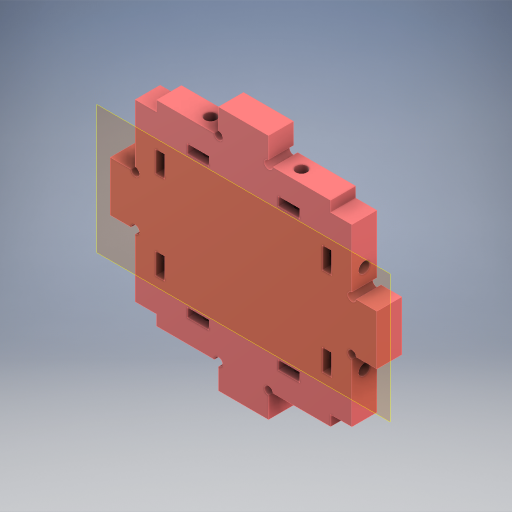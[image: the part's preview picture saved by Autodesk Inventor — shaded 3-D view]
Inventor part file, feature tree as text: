
AUTODESK INVENTOR PART (.ipt)
format: ipt  version: 2024 (Build 280153000, 153)  size: 487,936 bytes
history: native  units: in
note: dims shown in document units (in); Inventor stores cm internally (conversion verified against a paired STEP export)
features: extrude x6, sketch x6, other x4, reference x2, projected_geometry x1
ambient origin geometry x8: Origin, YZ Plane, XZ Plane, XY Plane, X Axis, Y Axis, Z Axis, Center Point
bodies: Body1 (feature_tree)
feature tree (19):
  other  "작업 평면1"
  extrude  "돌출9"  Depth=0.2756in
  extrude  "돌출10"  Depth=0.2756in
  extrude  "돌출11"  Depth=0.2756in
  extrude  "돌출12"  Depth=0.4724in
  extrude  "돌출13"  Depth=0.2362in
  extrude  "돌출14"  Depth=0.4724in
  sketch  "스케치1"
  reference  "참조1"
  reference  "참조2"
  sketch  "스케치7"
  sketch  "스케치8"
  sketch  "스케치9"
  sketch  "스케치10"
  sketch  "스케치11"
  projected_geometry  "투영된 루프3"
  other  "조립품2"
  other  "connection_leg:1"
  other  "connection_leg_64:1"
